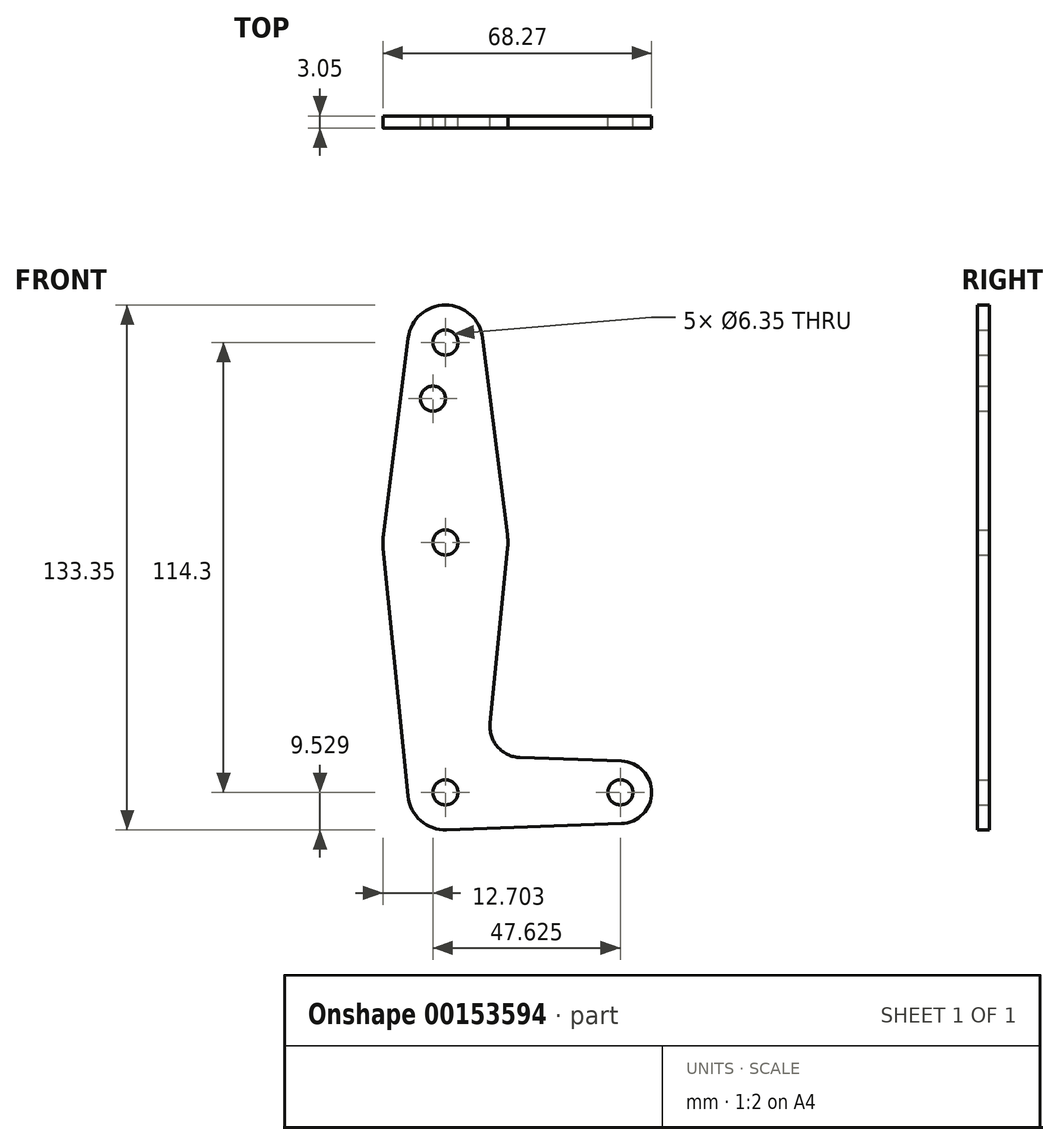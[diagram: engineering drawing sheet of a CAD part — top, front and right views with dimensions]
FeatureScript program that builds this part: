
annotation { "Feature Type Name" : "Feature", "Feature Type Description" : "" }
export const myFeature = defineFeature(function(context is Context, id is Id, definition is map)
    precondition{}
    {
        {
            var Q0;
            Q0=qCreatedBy(makeId("Front.planeOp"),FACE);
            var sketch = newSketch(context, id + "F0", { "sketchPlane" : qUnion([Q0])});
            skCircle(sketch, "E0", {"center": v(91.89, -107.47) * mm, "radius": 7.94 * mm});
            skLineSegment(sketch, "E1", {"start": v(91.89, -107.47) * mm, "end": v(47.44, -107.47) * mm, "construction": true});
            skLineSegment(sketch, "E2", {"start": v(47.44, -107.47) * mm, "end": v(47.44, -43.97) * mm, "construction": true});
            skLineSegment(sketch, "E3", {"start": v(47.44, -43.97) * mm, "end": v(47.44, 6.83) * mm, "construction": true});
            skCircle(sketch, "E4", {"center": v(47.44, 6.83) * mm, "radius": 9.53 * mm});
            skCircle(sketch, "E5", {"center": v(47.44, -43.97) * mm, "radius": 15.88 * mm});
            skCircle(sketch, "E6", {"center": v(47.44, -107.47) * mm, "radius": 9.53 * mm});
            skLineSegment(sketch, "E7", {"start": v(92.17, -115.4) * mm, "end": v(47.78, -117) * mm});
            skLineSegment(sketch, "E8", {"start": v(37.96, -108.42) * mm, "end": v(31.64, -45.56) * mm});
            skLineSegment(sketch, "E9", {"start": v(56.89, 8.02) * mm, "end": v(63.19, -41.99) * mm});
            skLineSegment(sketch, "E10", {"start": v(37.99, 8.02) * mm, "end": v(31.69, -41.99) * mm});
            skLineSegment(sketch, "E11", {"start": v(63.23, -45.56) * mm, "end": v(58.78, -89.88) * mm});
            skLineSegment(sketch, "E12", {"start": v(92.17, -99.54) * mm, "end": v(66.4, -98.62) * mm});
            skArc(sketch, "E13.filletArc", {"start": v(58.78, -89.88) * mm, "mid": v(60.7, -95.9) * mm, "end": v(66.4, -98.62) * mm});
            skLineSegment(sketch, "E14", {"start": v(47.44, -43.97) * mm, "end": v(47.44, -7.45) * mm, "construction": true});
            skCircle(sketch, "E15", {"center": v(44.26, -7.45) * mm, "radius": 3.18 * mm});
            skCircle(sketch, "E16", {"center": v(47.44, 6.83) * mm, "radius": 3.18 * mm});
            skCircle(sketch, "E17", {"center": v(47.44, -43.97) * mm, "radius": 3.18 * mm});
            skCircle(sketch, "E18", {"center": v(47.44, -107.47) * mm, "radius": 3.18 * mm});
            skCircle(sketch, "E19", {"center": v(91.89, -107.47) * mm, "radius": 3.18 * mm});
            skSolve(sketch);
        }
        {
            var Q0;
            {var subQ1=sQuery(id+"F0.wireOp",EDGE,"E9");Q0=makeQuery(id+"F0.imprint","IMPRINT",FACE,{"disambiguationData":[TD([[makeQuery(id+"F0.imprint","IMPRINT",EDGE,{"derivedFrom":subQ1}),-1.0]])]});}
            var Q1;
            Q1=makeQuery(id+"F0.imprint","IMPRINT",FACE,{"disambiguationData":[TD([[makeQuery(id+"F0.imprint","IMPRINT",EDGE,{"derivedFrom":sQuery(id+"F0.wireOp",EDGE,"E16")}),-1.0]])]});
            var Q2;
            Q2=makeQuery(id+"F0.imprint","IMPRINT",FACE,{"disambiguationData":[TD([[makeQuery(id+"F0.imprint","IMPRINT",EDGE,{"derivedFrom":sQuery(id+"F0.wireOp",EDGE,"E17")}),-1.0]])]});
            var Q3;
            {var subQ0=sQuery(id+"F0.wireOp",EDGE,"E7");Q3=makeQuery(id+"F0.imprint","IMPRINT",FACE,{"disambiguationData":[TD([[makeQuery(id+"F0.imprint","IMPRINT",EDGE,{"derivedFrom":subQ0}),-1.0]])]});}
            var Q4;
            Q4=makeQuery(id+"F0.imprint","IMPRINT",FACE,{"disambiguationData":[TD([[makeQuery(id+"F0.imprint","IMPRINT",EDGE,{"derivedFrom":sQuery(id+"F0.wireOp",EDGE,"E18")}),-1.0]])]});
            var Q5;
            Q5=makeQuery(id+"F0.imprint","IMPRINT",FACE,{"disambiguationData":[TD([[makeQuery(id+"F0.imprint","IMPRINT",EDGE,{"derivedFrom":sQuery(id+"F0.wireOp",EDGE,"E19")}),-1.0]])]});
            extrude(context, id + "F1", {"entities" : qUnion([Q0, Q1, Q2, Q3, Q4, Q5]), "depth" : 3.05 * mm});
        }
    });
